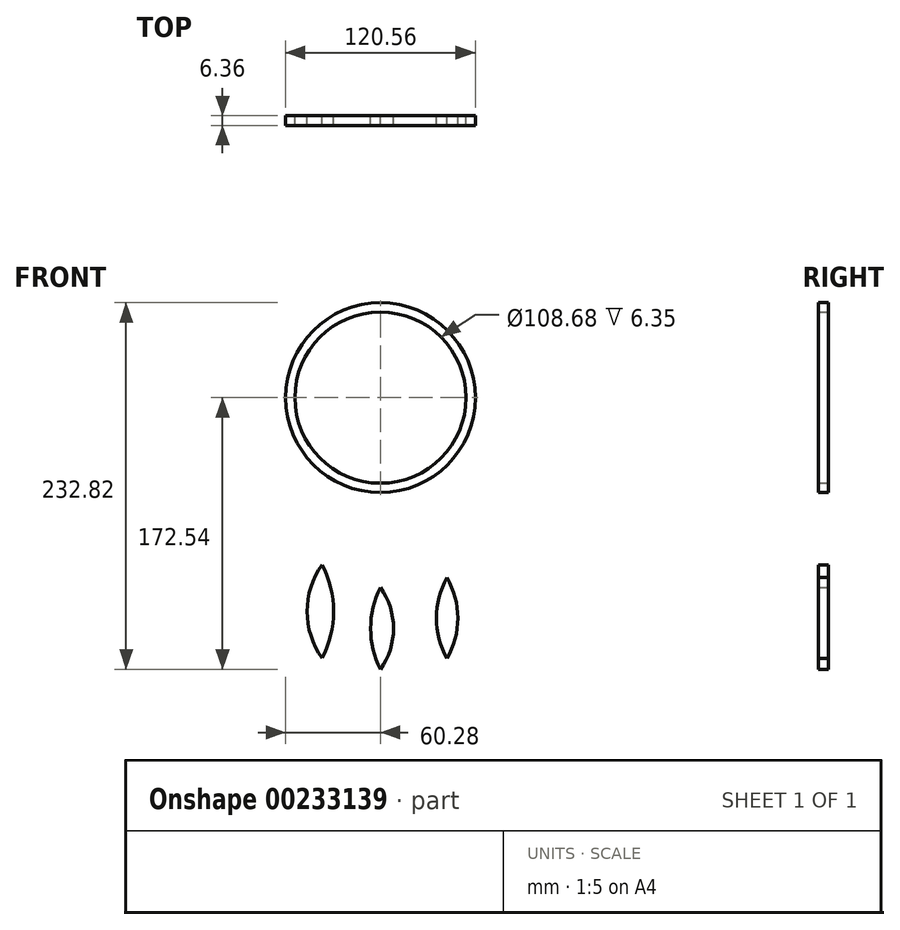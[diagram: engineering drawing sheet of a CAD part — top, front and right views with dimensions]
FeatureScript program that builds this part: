
annotation { "Feature Type Name" : "Feature", "Feature Type Description" : "" }
export const myFeature = defineFeature(function(context is Context, id is Id, definition is map)
    precondition{}
    {
        {
            var Q0;
            Q0=qCreatedBy(makeId("Front.planeOp"),FACE);
            var sketch = newSketch(context, id + "F0", { "sketchPlane" : qUnion([Q0])});
            skCircle(sketch, "E0", {"center": v(0, 0) * mm, "radius": 60.28 * mm});
            skCircle(sketch, "E1", {"center": v(0, 0) * mm, "radius": 54.34 * mm});
            skCircle(sketch, "E2.cCircle", {"center": v(0, 0) * mm, "radius": 54.34 * mm, "construction": true});
            skLineSegment(sketch, "E2.0", {"start": v(19.76, 50.62) * mm, "end": v(33.95, -42.43) * mm});
            skLineSegment(sketch, "E2.1", {"start": v(33.95, -42.43) * mm, "end": v(-53.72, -8.2) * mm});
            skLineSegment(sketch, "E2.2", {"start": v(-53.72, -8.2) * mm, "end": v(19.76, 50.62) * mm});
            skLineSegment(sketch, "E3.0", {"start": v(41.54, 35.03) * mm, "end": v(9.57, -53.49) * mm});
            skLineSegment(sketch, "E3.1", {"start": v(9.57, -53.49) * mm, "end": v(-51.1, 18.46) * mm});
            skLineSegment(sketch, "E3.2", {"start": v(-51.1, 18.46) * mm, "end": v(41.54, 35.03) * mm});
            skLineSegment(sketch, "E4.0", {"start": v(48.74, 24.02) * mm, "end": v(-3.57, -54.22) * mm});
            skLineSegment(sketch, "E4.1", {"start": v(-3.57, -54.22) * mm, "end": v(-45.17, 30.2) * mm});
            skLineSegment(sketch, "E4.2", {"start": v(-45.17, 30.2) * mm, "end": v(48.74, 24.02) * mm});
            skLineSegment(sketch, "E5.0", {"start": v(0, 54.34) * mm, "end": v(47.06, -27.17) * mm});
            skLineSegment(sketch, "E5.1", {"start": v(47.06, -27.17) * mm, "end": v(-47.06, -27.17) * mm});
            skLineSegment(sketch, "E5.2", {"start": v(-47.06, -27.17) * mm, "end": v(0, 54.34) * mm});
            skLineSegment(sketch, "E6.0", {"start": v(-16.13, 51.89) * mm, "end": v(53, -11.97) * mm});
            skLineSegment(sketch, "E6.1", {"start": v(53, -11.97) * mm, "end": v(-36.87, -39.92) * mm});
            skLineSegment(sketch, "E6.2", {"start": v(-36.87, -39.92) * mm, "end": v(-16.13, 51.89) * mm});
            skLineSegment(sketch, "E7.0", {"start": v(-32.63, 43.45) * mm, "end": v(53.95, 6.53) * mm});
            skLineSegment(sketch, "E7.1", {"start": v(53.95, 6.53) * mm, "end": v(-21.31, -49.98) * mm});
            skLineSegment(sketch, "E7.2", {"start": v(-21.31, -49.98) * mm, "end": v(-32.63, 43.45) * mm});
            skLineSegment(sketch, "E8.0", {"start": v(31.06, 44.59) * mm, "end": v(23.08, -49.2) * mm});
            skLineSegment(sketch, "E8.1", {"start": v(23.08, -49.2) * mm, "end": v(-54.14, 4.6) * mm});
            skLineSegment(sketch, "E8.2", {"start": v(-54.14, 4.6) * mm, "end": v(31.06, 44.59) * mm});
            skCircle(sketch, "E9", {"center": v(0, 0) * mm, "radius": 27.18 * mm});
            skCircle(sketch, "E10.cCircle", {"center": v(0, 0) * mm, "radius": 27.18 * mm, "construction": true});
            skLineSegment(sketch, "E10.0", {"start": v(2.67, 27.05) * mm, "end": v(22.1, -15.84) * mm});
            skLineSegment(sketch, "E10.1", {"start": v(22.1, -15.84) * mm, "end": v(-24.76, -11.21) * mm});
            skLineSegment(sketch, "E10.2", {"start": v(-24.76, -11.21) * mm, "end": v(2.67, 27.05) * mm});
            skCircle(sketch, "E11.cCircle", {"center": v(0, 0) * mm, "radius": 27.17 * mm, "construction": true});
            skLineSegment(sketch, "E11.0", {"start": v(10.66, 25) * mm, "end": v(16.32, -21.73) * mm});
            skLineSegment(sketch, "E11.1", {"start": v(16.32, -21.73) * mm, "end": v(-26.97, -3.27) * mm});
            skLineSegment(sketch, "E11.2", {"start": v(-26.97, -3.27) * mm, "end": v(10.66, 25) * mm});
            skLineSegment(sketch, "E12.0", {"start": v(17.78, 20.56) * mm, "end": v(8.91, -25.68) * mm});
            skLineSegment(sketch, "E12.1", {"start": v(8.91, -25.68) * mm, "end": v(-26.7, 5.12) * mm});
            skLineSegment(sketch, "E12.2", {"start": v(-26.7, 5.12) * mm, "end": v(17.78, 20.56) * mm});
            skLineSegment(sketch, "E13.0", {"start": v(22.3, 15.51) * mm, "end": v(2.28, -27.07) * mm});
            skLineSegment(sketch, "E13.1", {"start": v(2.28, -27.07) * mm, "end": v(-24.59, 11.56) * mm});
            skLineSegment(sketch, "E13.2", {"start": v(-24.59, 11.56) * mm, "end": v(22.3, 15.51) * mm});
            skLineSegment(sketch, "E14.0", {"start": v(26.04, 7.75) * mm, "end": v(-6.3, -26.43) * mm});
            skLineSegment(sketch, "E14.1", {"start": v(-6.3, -26.43) * mm, "end": v(-19.73, 18.68) * mm});
            skLineSegment(sketch, "E14.2", {"start": v(-19.73, 18.68) * mm, "end": v(26.04, 7.75) * mm});
            skLineSegment(sketch, "E15.0", {"start": v(27.18, 0) * mm, "end": v(-13.6, -23.54) * mm});
            skLineSegment(sketch, "E15.1", {"start": v(-13.6, -23.54) * mm, "end": v(-13.6, 23.54) * mm});
            skLineSegment(sketch, "E15.2", {"start": v(-13.6, 23.54) * mm, "end": v(27.18, 0) * mm});
            skLineSegment(sketch, "E16.0", {"start": v(26.17, -7.31) * mm, "end": v(-19.42, -19) * mm});
            skLineSegment(sketch, "E16.1", {"start": v(-19.42, -19) * mm, "end": v(-6.75, 26.32) * mm});
            skLineSegment(sketch, "E16.2", {"start": v(-6.75, 26.32) * mm, "end": v(26.17, -7.31) * mm});
            skCircle(sketch, "E17", {"center": v(0, 0) * mm, "radius": 13.58 * mm});
            skCircle(sketch, "E18.cCircle", {"center": v(0, 0) * mm, "radius": 13.58 * mm, "construction": true});
            skLineSegment(sketch, "E18.0", {"start": v(3.15, 13.21) * mm, "end": v(9.87, -9.34) * mm});
            skLineSegment(sketch, "E18.1", {"start": v(9.87, -9.34) * mm, "end": v(-13.02, -3.88) * mm});
            skLineSegment(sketch, "E18.2", {"start": v(-13.02, -3.88) * mm, "end": v(3.15, 13.21) * mm});
            skCircle(sketch, "E19.cCircle", {"center": v(0, 0) * mm, "radius": 13.6 * mm, "construction": true});
            skLineSegment(sketch, "E19.0", {"start": v(6.8, 11.77) * mm, "end": v(6.8, -11.77) * mm});
            skLineSegment(sketch, "E19.1", {"start": v(6.8, -11.77) * mm, "end": v(-13.6, 0) * mm});
            skLineSegment(sketch, "E19.2", {"start": v(-13.6, 0) * mm, "end": v(6.8, 11.77) * mm});
            skLineSegment(sketch, "E20.0", {"start": v(9.87, 9.35) * mm, "end": v(3.16, -13.22) * mm});
            skLineSegment(sketch, "E20.1", {"start": v(3.16, -13.22) * mm, "end": v(-13.03, 3.87) * mm});
            skLineSegment(sketch, "E20.2", {"start": v(-13.03, 3.87) * mm, "end": v(9.87, 9.35) * mm});
            skLineSegment(sketch, "E21.0", {"start": v(12.38, 5.6) * mm, "end": v(-1.33, -13.53) * mm});
            skLineSegment(sketch, "E21.1", {"start": v(-1.33, -13.53) * mm, "end": v(-11.05, 7.92) * mm});
            skLineSegment(sketch, "E21.2", {"start": v(-11.05, 7.92) * mm, "end": v(12.38, 5.6) * mm});
            skCircle(sketch, "E22.cCircle", {"center": v(0, 0) * mm, "radius": 13.68 * mm, "construction": true});
            skLineSegment(sketch, "E22.0", {"start": v(13.68, 0) * mm, "end": v(-6.84, -11.85) * mm});
            skLineSegment(sketch, "E22.1", {"start": v(-6.84, -11.85) * mm, "end": v(-6.84, 11.85) * mm});
            skLineSegment(sketch, "E22.2", {"start": v(-6.84, 11.85) * mm, "end": v(13.68, 0) * mm});
            skPoint(sketch, "E23.cCircle.perimeterSnap0", {"position": v(12.3, -5.78) * mm});
            skLineSegment(sketch, "E23.0", {"start": v(12.3, -5.8) * mm, "end": v(-11.17, -7.75) * mm});
            skPoint(sketch, "E23.0.startSnap0", {"position": v(12.3, -5.78) * mm});
            skLineSegment(sketch, "E23.1", {"start": v(-11.17, -7.75) * mm, "end": v(-1.13, 13.55) * mm});
            skLineSegment(sketch, "E23.2", {"start": v(-1.13, 13.55) * mm, "end": v(12.3, -5.8) * mm});
            skCircle(sketch, "E24", {"center": v(0, 0) * mm, "radius": 6.84 * mm});
            skCircle(sketch, "E25.cCircle", {"center": v(0, 0) * mm, "radius": 6.84 * mm, "construction": true});
            skLineSegment(sketch, "E25.0", {"start": v(0, 6.84) * mm, "end": v(5.93, -3.42) * mm});
            skLineSegment(sketch, "E25.1", {"start": v(5.93, -3.42) * mm, "end": v(-5.93, -3.42) * mm});
            skLineSegment(sketch, "E25.2", {"start": v(-5.93, -3.42) * mm, "end": v(0, 6.84) * mm});
            skLineSegment(sketch, "E26", {"start": v(-34.21, -49.63) * mm, "end": v(-37.08, -106.15) * mm});
            skLineSegment(sketch, "E27", {"start": v(0, -60.28) * mm, "end": v(0, -120.7) * mm});
            skLineSegment(sketch, "E28", {"start": v(33.32, -50.24) * mm, "end": v(42.08, -114.31) * mm});
            skArc(sketch, "E29", {"start": v(-37.08, -165.43) * mm, "mid": v(-29.75, -135.8) * mm, "end": v(-37.08, -106.15) * mm});
            skArc(sketch, "E30", {"start": v(-37.08, -106.15) * mm, "mid": v(-46.6, -135.8) * mm, "end": v(-37.08, -165.43) * mm});
            skArc(sketch, "E31", {"start": v(0, -172.54) * mm, "mid": v(8.27, -146.62) * mm, "end": v(0, -120.7) * mm});
            skArc(sketch, "E32", {"start": v(0, -120.7) * mm, "mid": v(-6.27, -146.62) * mm, "end": v(0, -172.54) * mm});
            skArc(sketch, "E33", {"start": v(42.08, -165.77) * mm, "mid": v(49.12, -140.04) * mm, "end": v(42.08, -114.31) * mm});
            skArc(sketch, "E34", {"start": v(42.08, -114.31) * mm, "mid": v(35.58, -140.04) * mm, "end": v(42.08, -165.77) * mm});
            skLineSegment(sketch, "E35", {"start": v(-37.08, -106.15) * mm, "end": v(-37.08, -165.43) * mm});
            skLineSegment(sketch, "E36", {"start": v(0, -120.7) * mm, "end": v(0, -172.54) * mm});
            skLineSegment(sketch, "E37", {"start": v(42.08, -114.31) * mm, "end": v(42.08, -165.77) * mm});
            skSolve(sketch);
        }
        {
            var Q0;
            Q0 = qSketchRegion(id + "F0", true);
            extrude(context, id + "F1", {"entities" : qUnion([Q0]), "endBound" : BoundingType.SYMMETRIC, "depth" : 6.35 * mm});
        }
    });
